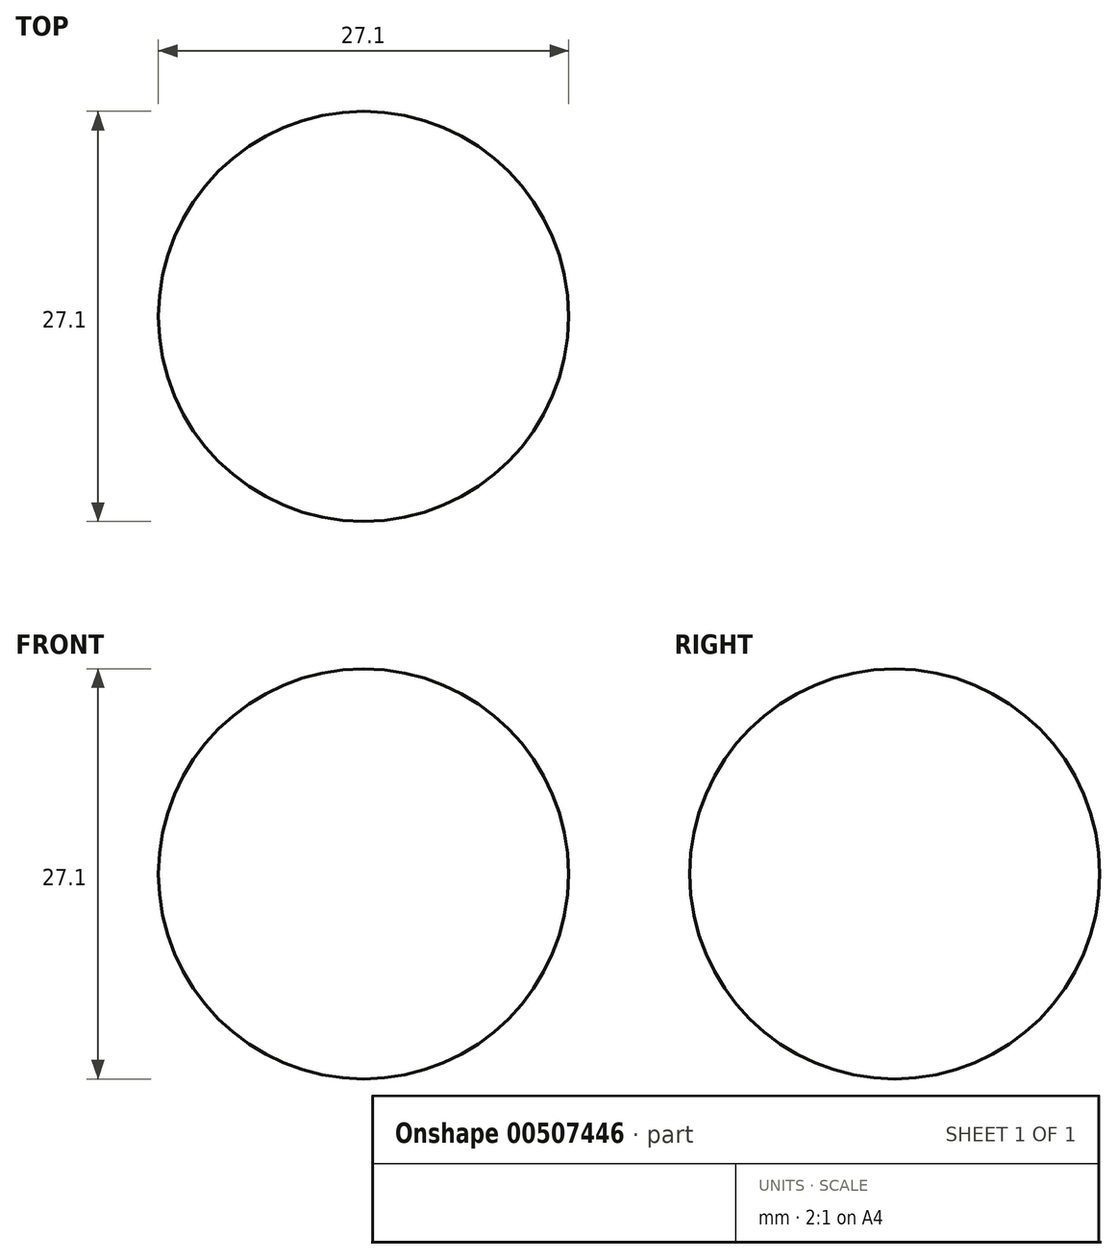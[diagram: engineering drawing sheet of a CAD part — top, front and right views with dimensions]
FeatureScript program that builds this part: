
annotation { "Feature Type Name" : "Feature", "Feature Type Description" : "" }
export const myFeature = defineFeature(function(context is Context, id is Id, definition is map)
    precondition{}
    {
        {
            var Q0;
            Q0=qCreatedBy(makeId("Front.planeOp"),FACE);
            var sketch = newSketch(context, id + "F0", { "sketchPlane" : qUnion([Q0])});
            skArc(sketch, "E0", {"start": v(13.55, 0) * mm, "mid": v(0, 13.55) * mm, "end": v(-13.55, 0) * mm});
            skLineSegment(sketch, "E1", {"start": v(-13.55, 0) * mm, "end": v(13.55, 0) * mm});
            skSolve(sketch);
        }
        {
            var Q0;
            Q0=makeQuery(id+"F0.imprint","IMPRINT",FACE,{"disambiguationData":[TD([[makeQuery(id+"F0.imprint","IMPRINT",EDGE,{"derivedFrom":sQuery(id+"F0.wireOp",EDGE,"E0")}),1.0]])]});
            var Q1;
            Q1=sQuery(id+"F0.wireOp",EDGE,"E1");
            revolve(context, id + "F1", {"entities" : qUnion([Q0]), "axis" : qUnion([Q1]), "revolveType" : RevolveType.FULL});
        }
    });
